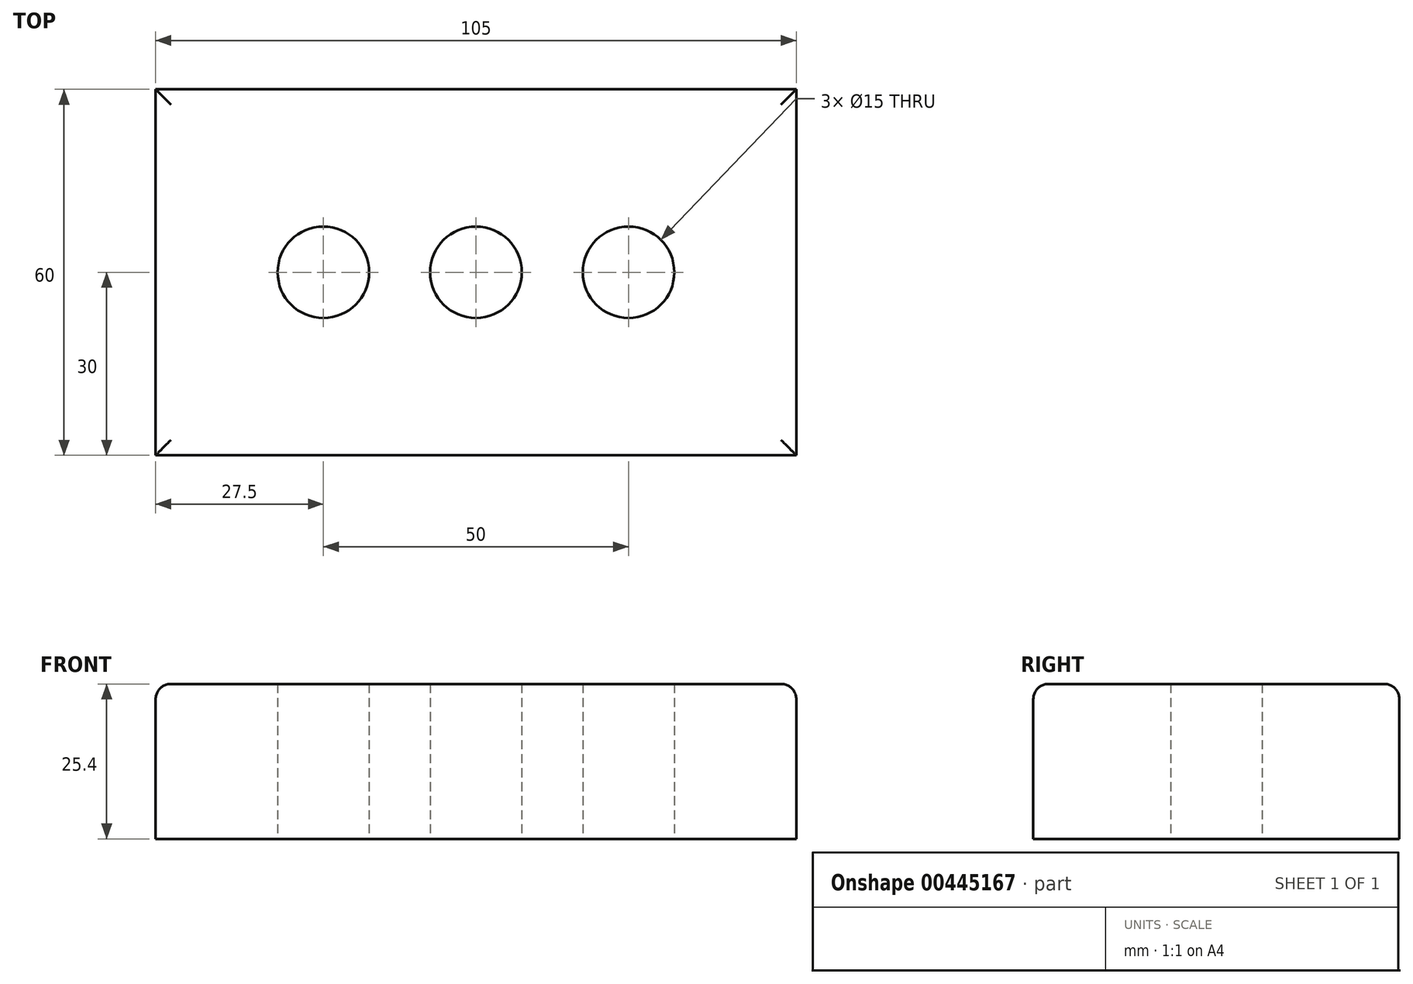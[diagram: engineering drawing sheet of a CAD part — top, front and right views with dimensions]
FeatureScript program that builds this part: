
annotation { "Feature Type Name" : "Feature", "Feature Type Description" : "" }
export const myFeature = defineFeature(function(context is Context, id is Id, definition is map)
    precondition{}
    {
        {
            var Q0;
            Q0=qCreatedBy(makeId("Top.planeOp"),FACE);
            var sketch = newSketch(context, id + "F0", { "sketchPlane" : qUnion([Q0])});
            skLineSegment(sketch, "E0.bottom", {"start": v(52.5, 30) * mm, "end": v(-52.5, 30) * mm});
            skLineSegment(sketch, "E0.top", {"start": v(52.5, -30) * mm, "end": v(-52.5, -30) * mm});
            skLineSegment(sketch, "E0.left", {"start": v(52.5, 30) * mm, "end": v(52.5, -30) * mm});
            skLineSegment(sketch, "E0.right", {"start": v(-52.5, 30) * mm, "end": v(-52.5, -30) * mm});
            skPoint(sketch, "E0.middle", {"position": v(0, 0) * mm});
            skCircle(sketch, "E1", {"center": v(0, 0) * mm, "radius": 7.5 * mm});
            skLineSegment(sketch, "E2", {"start": v(-17.5, 0) * mm, "end": v(-7.5, 0) * mm});
            skCircle(sketch, "E3", {"center": v(-25, 0) * mm, "radius": 7.5 * mm});
            skCircle(sketch, "E4.MirrorC", {"center": v(25, 0) * mm, "radius": 7.5 * mm});
            skSolve(sketch);
        }
        {
            var Q0;
            Q0 = qSketchRegion(id + "F0", true);
            extrude(context, id + "F1", {"entities" : qUnion([Q0]), "depth" : 20 * mm});
        }
        {
            var Q0;
            Q0 = qSketchRegion(id + "F0", true);
            extrude(context, id + "F2", {"entities" : qUnion([Q0]), "operationType" : NewBodyOperationType.ADD, "depth" : 25.4 * mm});
        }
        {
            var Q0;
            Q0=makeQuery(id+"F2.opExtrude","CAP_EDGE",EDGE,{"disambiguationData":[OSD([sQuery(id+"F0.wireOp",EDGE,"E0.top")])],"isStart":false});
            var Q1;
            Q1=makeQuery(id+"F2.opExtrude","CAP_EDGE",EDGE,{"disambiguationData":[OSD([sQuery(id+"F0.wireOp",EDGE,"E0.right")])],"isStart":false});
            var Q2;
            Q2=makeQuery(id+"F2.opExtrude","CAP_EDGE",EDGE,{"disambiguationData":[OSD([sQuery(id+"F0.wireOp",EDGE,"E0.bottom")])],"isStart":false});
            var Q3;
            Q3=makeQuery(id+"F2.opExtrude","CAP_EDGE",EDGE,{"disambiguationData":[OSD([sQuery(id+"F0.wireOp",EDGE,"E0.left")])],"isStart":false});
            fillet(context, id + "F3", {"entities" : qUnion([Q0, Q1, Q2, Q3]), "radius" : 2.5 * mm, "tangentPropagation" : true, "allowEdgeOverflow" : false});
        }
    });
